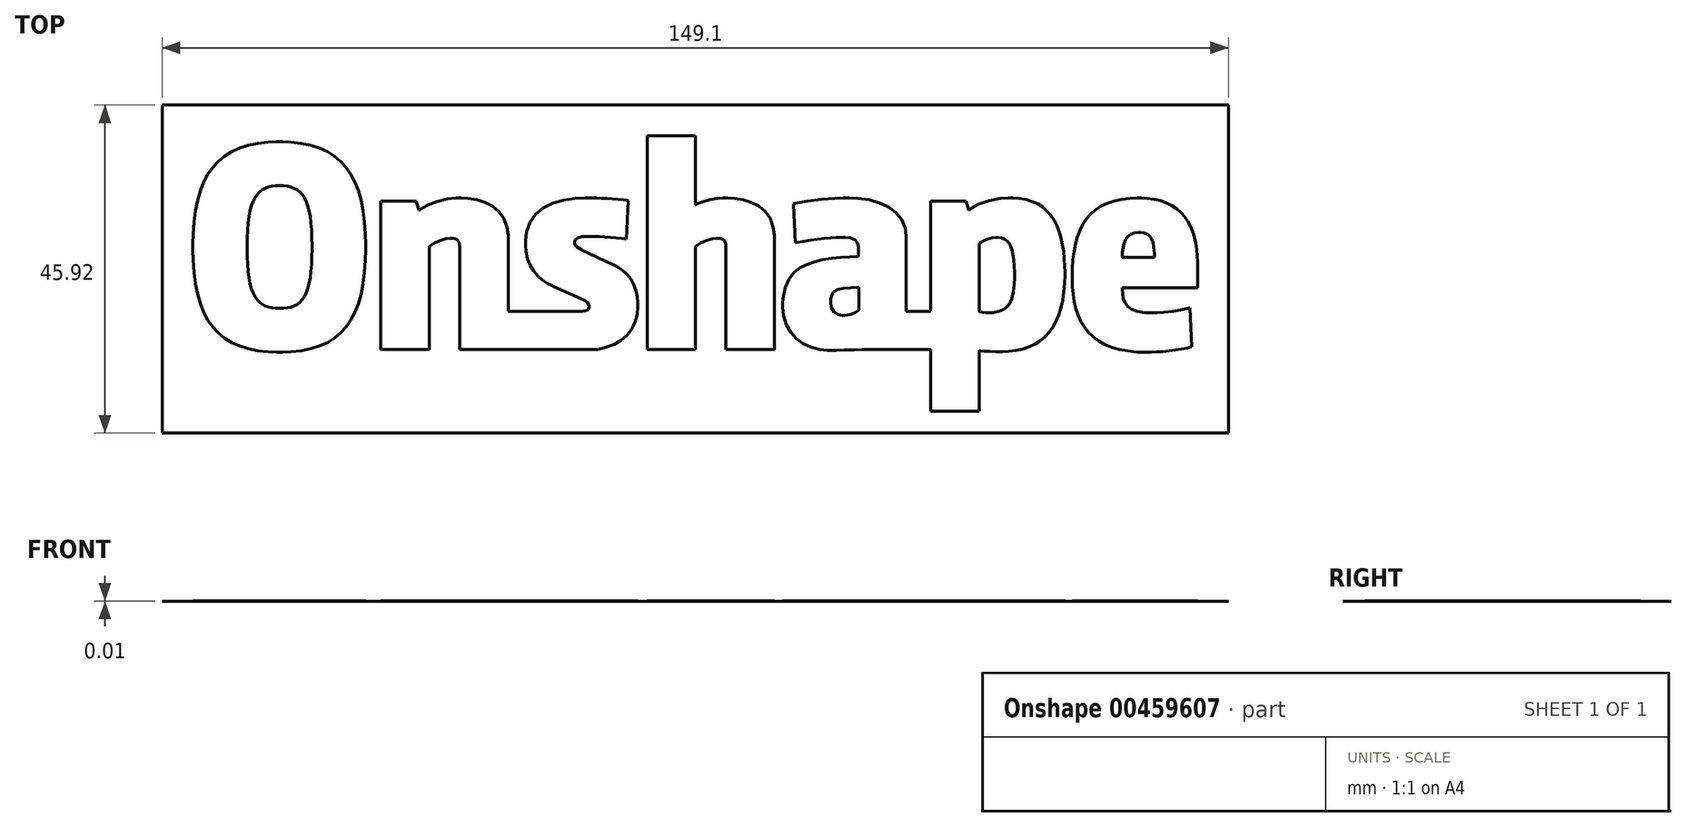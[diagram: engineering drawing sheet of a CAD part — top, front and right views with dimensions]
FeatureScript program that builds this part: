
annotation { "Feature Type Name" : "Feature", "Feature Type Description" : "" }
export const myFeature = defineFeature(function(context is Context, id is Id, definition is map)
    precondition{}
    {
        {
            assignVariable(context, id + "F0", {"name" : "plateHeight", "anyValue" : 1 / 203.2 * mm});
        }
        {
            assignVariable(context, id + "F1", {"name" : "letterHeight", "anyValue" : getVariable(context, 'plateHeight') + (1 / 406.4 * mm)});
        }
        {
            assignVariable(context, id + "F2", {"name" : "scaleFactor", "anyValue" : .226});
        }
        {
            var Q0;
            Q0=qCreatedBy(makeId("Top.planeOp"),FACE);
            var sketch = newSketch(context, id + "F3", { "sketchPlane" : qUnion([Q0])});
            skLineSegment(sketch, "E0", {"start": v(-257.2, 81.58) * mm, "end": v(-258.95, 81.58) * mm});
            skLineSegment(sketch, "E1", {"start": v(-258.95, 81.58) * mm, "end": v(-264.22, 81.33) * mm});
            skLineSegment(sketch, "E2", {"start": v(-264.22, 81.33) * mm, "end": v(-270.7, 80.6) * mm});
            skLineSegment(sketch, "E3", {"start": v(-270.7, 80.6) * mm, "end": v(-276.63, 79.38) * mm});
            skLineSegment(sketch, "E4", {"start": v(-276.63, 79.38) * mm, "end": v(-282.03, 77.66) * mm});
            skLineSegment(sketch, "E5", {"start": v(-282.03, 77.66) * mm, "end": v(-286.92, 75.43) * mm});
            skLineSegment(sketch, "E6", {"start": v(-286.92, 75.43) * mm, "end": v(-291.3, 72.7) * mm});
            skLineSegment(sketch, "E7", {"start": v(-291.3, 72.7) * mm, "end": v(-295.2, 69.45) * mm});
            skLineSegment(sketch, "E8", {"start": v(-295.2, 69.45) * mm, "end": v(-298.64, 65.69) * mm});
            skLineSegment(sketch, "E9", {"start": v(-298.64, 65.69) * mm, "end": v(-301.61, 61.4) * mm});
            skLineSegment(sketch, "E10", {"start": v(-301.61, 61.4) * mm, "end": v(-304.14, 56.58) * mm});
            skLineSegment(sketch, "E11", {"start": v(-304.14, 56.58) * mm, "end": v(-306.24, 51.23) * mm});
            skLineSegment(sketch, "E12", {"start": v(-306.24, 51.23) * mm, "end": v(-307.93, 45.34) * mm});
            skLineSegment(sketch, "E13", {"start": v(-307.93, 45.34) * mm, "end": v(-309.22, 38.91) * mm});
            skLineSegment(sketch, "E14", {"start": v(-309.22, 38.91) * mm, "end": v(-310.12, 31.93) * mm});
            skLineSegment(sketch, "E15", {"start": v(-310.12, 31.93) * mm, "end": v(-310.65, 24.4) * mm});
            skLineSegment(sketch, "E16", {"start": v(-310.65, 24.4) * mm, "end": v(-310.83, 18.34) * mm});
            skLineSegment(sketch, "E17", {"start": v(-310.83, 18.34) * mm, "end": v(-310.83, 16.31) * mm});
            skLineSegment(sketch, "E18", {"start": v(-310.83, 16.31) * mm, "end": v(-310.83, 14.3) * mm});
            skLineSegment(sketch, "E19", {"start": v(-310.83, 14.3) * mm, "end": v(-310.65, 8.23) * mm});
            skLineSegment(sketch, "E20", {"start": v(-310.65, 8.23) * mm, "end": v(-310.12, 0.7) * mm});
            skLineSegment(sketch, "E21", {"start": v(-310.12, 0.7) * mm, "end": v(-309.22, -6.26) * mm});
            skLineSegment(sketch, "E22", {"start": v(-309.22, -6.26) * mm, "end": v(-307.93, -12.69) * mm});
            skLineSegment(sketch, "E23", {"start": v(-307.93, -12.69) * mm, "end": v(-306.24, -18.56) * mm});
            skLineSegment(sketch, "E24", {"start": v(-306.24, -18.56) * mm, "end": v(-304.14, -23.89) * mm});
            skLineSegment(sketch, "E25", {"start": v(-304.14, -23.89) * mm, "end": v(-301.61, -28.7) * mm});
            skLineSegment(sketch, "E26", {"start": v(-301.61, -28.7) * mm, "end": v(-298.64, -32.96) * mm});
            skLineSegment(sketch, "E27", {"start": v(-298.64, -32.96) * mm, "end": v(-295.2, -36.7) * mm});
            skLineSegment(sketch, "E28", {"start": v(-295.2, -36.7) * mm, "end": v(-291.3, -39.94) * mm});
            skLineSegment(sketch, "E29", {"start": v(-291.3, -39.94) * mm, "end": v(-286.92, -42.66) * mm});
            skLineSegment(sketch, "E30", {"start": v(-286.92, -42.66) * mm, "end": v(-282.03, -44.87) * mm});
            skLineSegment(sketch, "E31", {"start": v(-282.03, -44.87) * mm, "end": v(-276.63, -46.58) * mm});
            skLineSegment(sketch, "E32", {"start": v(-276.63, -46.58) * mm, "end": v(-270.7, -47.8) * mm});
            skLineSegment(sketch, "E33", {"start": v(-270.7, -47.8) * mm, "end": v(-264.22, -48.52) * mm});
            skLineSegment(sketch, "E34", {"start": v(-264.22, -48.52) * mm, "end": v(-258.95, -48.76) * mm});
            skLineSegment(sketch, "E35", {"start": v(-258.95, -48.76) * mm, "end": v(-257.2, -48.76) * mm});
            skLineSegment(sketch, "E36", {"start": v(-257.2, -48.76) * mm, "end": v(-255.44, -48.76) * mm});
            skLineSegment(sketch, "E37", {"start": v(-255.44, -48.76) * mm, "end": v(-250.2, -48.52) * mm});
            skLineSegment(sketch, "E38", {"start": v(-250.2, -48.52) * mm, "end": v(-243.76, -47.8) * mm});
            skLineSegment(sketch, "E39", {"start": v(-243.76, -47.8) * mm, "end": v(-237.86, -46.58) * mm});
            skLineSegment(sketch, "E40", {"start": v(-237.86, -46.58) * mm, "end": v(-232.5, -44.87) * mm});
            skLineSegment(sketch, "E41", {"start": v(-232.5, -44.87) * mm, "end": v(-227.64, -42.66) * mm});
            skLineSegment(sketch, "E42", {"start": v(-227.64, -42.66) * mm, "end": v(-223.28, -39.94) * mm});
            skLineSegment(sketch, "E43", {"start": v(-223.28, -39.94) * mm, "end": v(-219.4, -36.7) * mm});
            skLineSegment(sketch, "E44", {"start": v(-219.4, -36.7) * mm, "end": v(-216, -32.96) * mm});
            skLineSegment(sketch, "E45", {"start": v(-216, -32.96) * mm, "end": v(-213.05, -28.7) * mm});
            skLineSegment(sketch, "E46", {"start": v(-213.05, -28.7) * mm, "end": v(-210.55, -23.89) * mm});
            skLineSegment(sketch, "E47", {"start": v(-210.55, -23.89) * mm, "end": v(-208.46, -18.56) * mm});
            skLineSegment(sketch, "E48", {"start": v(-208.46, -18.56) * mm, "end": v(-206.8, -12.69) * mm});
            skLineSegment(sketch, "E49", {"start": v(-206.8, -12.69) * mm, "end": v(-205.52, -6.26) * mm});
            skLineSegment(sketch, "E50", {"start": v(-205.52, -6.26) * mm, "end": v(-204.63, 0.7) * mm});
            skLineSegment(sketch, "E51", {"start": v(-204.63, 0.7) * mm, "end": v(-204.1, 8.23) * mm});
            skLineSegment(sketch, "E52", {"start": v(-204.1, 8.23) * mm, "end": v(-203.93, 14.3) * mm});
            skLineSegment(sketch, "E53", {"start": v(-203.93, 14.3) * mm, "end": v(-203.93, 16.31) * mm});
            skLineSegment(sketch, "E54", {"start": v(-203.93, 16.31) * mm, "end": v(-203.93, 18.34) * mm});
            skLineSegment(sketch, "E55", {"start": v(-203.93, 18.34) * mm, "end": v(-204.1, 24.4) * mm});
            skLineSegment(sketch, "E56", {"start": v(-204.1, 24.4) * mm, "end": v(-204.63, 31.93) * mm});
            skLineSegment(sketch, "E57", {"start": v(-204.63, 31.93) * mm, "end": v(-205.52, 38.91) * mm});
            skLineSegment(sketch, "E58", {"start": v(-205.52, 38.91) * mm, "end": v(-206.8, 45.34) * mm});
            skLineSegment(sketch, "E59", {"start": v(-206.8, 45.34) * mm, "end": v(-208.46, 51.23) * mm});
            skLineSegment(sketch, "E60", {"start": v(-208.46, 51.23) * mm, "end": v(-210.55, 56.58) * mm});
            skLineSegment(sketch, "E61", {"start": v(-210.55, 56.58) * mm, "end": v(-213.05, 61.4) * mm});
            skLineSegment(sketch, "E62", {"start": v(-213.05, 61.4) * mm, "end": v(-216, 65.69) * mm});
            skLineSegment(sketch, "E63", {"start": v(-216, 65.69) * mm, "end": v(-219.4, 69.45) * mm});
            skLineSegment(sketch, "E64", {"start": v(-219.4, 69.45) * mm, "end": v(-223.28, 72.7) * mm});
            skLineSegment(sketch, "E65", {"start": v(-223.28, 72.7) * mm, "end": v(-227.64, 75.43) * mm});
            skLineSegment(sketch, "E66", {"start": v(-227.64, 75.43) * mm, "end": v(-232.5, 77.66) * mm});
            skLineSegment(sketch, "E67", {"start": v(-232.5, 77.66) * mm, "end": v(-237.86, 79.38) * mm});
            skLineSegment(sketch, "E68", {"start": v(-237.86, 79.38) * mm, "end": v(-243.76, 80.6) * mm});
            skLineSegment(sketch, "E69", {"start": v(-243.76, 80.6) * mm, "end": v(-250.2, 81.33) * mm});
            skLineSegment(sketch, "E70", {"start": v(-250.2, 81.33) * mm, "end": v(-255.44, 81.58) * mm});
            skLineSegment(sketch, "E71", {"start": v(-255.44, 81.58) * mm, "end": v(-257.2, 81.58) * mm});
            skLineSegment(sketch, "E72", {"start": v(-257.2, -21.57) * mm, "end": v(-257.83, -21.57) * mm});
            skLineSegment(sketch, "E73", {"start": v(-257.83, -21.57) * mm, "end": v(-259.73, -21.48) * mm});
            skLineSegment(sketch, "E74", {"start": v(-259.73, -21.48) * mm, "end": v(-262.1, -21.2) * mm});
            skLineSegment(sketch, "E75", {"start": v(-262.1, -21.2) * mm, "end": v(-264.27, -20.73) * mm});
            skLineSegment(sketch, "E76", {"start": v(-264.27, -20.73) * mm, "end": v(-266.26, -20) * mm});
            skLineSegment(sketch, "E77", {"start": v(-266.26, -20) * mm, "end": v(-268.08, -19.01) * mm});
            skLineSegment(sketch, "E78", {"start": v(-268.08, -19.01) * mm, "end": v(-269.72, -17.74) * mm});
            skLineSegment(sketch, "E79", {"start": v(-269.72, -17.74) * mm, "end": v(-271.2, -16.15) * mm});
            skLineSegment(sketch, "E80", {"start": v(-271.2, -16.15) * mm, "end": v(-272.5, -14.23) * mm});
            skLineSegment(sketch, "E81", {"start": v(-272.5, -14.23) * mm, "end": v(-273.64, -11.94) * mm});
            skLineSegment(sketch, "E82", {"start": v(-273.64, -11.94) * mm, "end": v(-274.62, -9.27) * mm});
            skLineSegment(sketch, "E83", {"start": v(-274.62, -9.27) * mm, "end": v(-275.44, -6.18) * mm});
            skLineSegment(sketch, "E84", {"start": v(-275.44, -6.18) * mm, "end": v(-276.1, -2.66) * mm});
            skLineSegment(sketch, "E85", {"start": v(-276.1, -2.66) * mm, "end": v(-276.6, 1.33) * mm});
            skLineSegment(sketch, "E86", {"start": v(-276.6, 1.33) * mm, "end": v(-276.97, 5.8) * mm});
            skLineSegment(sketch, "E87", {"start": v(-276.97, 5.8) * mm, "end": v(-277.19, 10.79) * mm});
            skLineSegment(sketch, "E88", {"start": v(-277.19, 10.79) * mm, "end": v(-277.26, 14.93) * mm});
            skLineSegment(sketch, "E89", {"start": v(-277.26, 14.93) * mm, "end": v(-277.26, 16.31) * mm});
            skLineSegment(sketch, "E90", {"start": v(-277.26, 16.31) * mm, "end": v(-277.26, 17.7) * mm});
            skLineSegment(sketch, "E91", {"start": v(-277.26, 17.7) * mm, "end": v(-277.19, 21.84) * mm});
            skLineSegment(sketch, "E92", {"start": v(-277.19, 21.84) * mm, "end": v(-276.97, 26.83) * mm});
            skLineSegment(sketch, "E93", {"start": v(-276.97, 26.83) * mm, "end": v(-276.6, 31.32) * mm});
            skLineSegment(sketch, "E94", {"start": v(-276.6, 31.32) * mm, "end": v(-276.1, 35.32) * mm});
            skLineSegment(sketch, "E95", {"start": v(-276.1, 35.32) * mm, "end": v(-275.44, 38.86) * mm});
            skLineSegment(sketch, "E96", {"start": v(-275.44, 38.86) * mm, "end": v(-274.62, 41.96) * mm});
            skLineSegment(sketch, "E97", {"start": v(-274.62, 41.96) * mm, "end": v(-273.64, 44.65) * mm});
            skLineSegment(sketch, "E98", {"start": v(-273.64, 44.65) * mm, "end": v(-272.5, 46.96) * mm});
            skLineSegment(sketch, "E99", {"start": v(-272.5, 46.96) * mm, "end": v(-271.2, 48.9) * mm});
            skLineSegment(sketch, "E100", {"start": v(-271.2, 48.9) * mm, "end": v(-269.72, 50.5) * mm});
            skLineSegment(sketch, "E101", {"start": v(-269.72, 50.5) * mm, "end": v(-268.08, 51.79) * mm});
            skLineSegment(sketch, "E102", {"start": v(-268.08, 51.79) * mm, "end": v(-266.26, 52.8) * mm});
            skLineSegment(sketch, "E103", {"start": v(-266.26, 52.8) * mm, "end": v(-264.27, 53.52) * mm});
            skLineSegment(sketch, "E104", {"start": v(-264.27, 53.52) * mm, "end": v(-262.1, 54.02) * mm});
            skLineSegment(sketch, "E105", {"start": v(-262.1, 54.02) * mm, "end": v(-259.73, 54.3) * mm});
            skLineSegment(sketch, "E106", {"start": v(-259.73, 54.3) * mm, "end": v(-257.83, 54.39) * mm});
            skLineSegment(sketch, "E107", {"start": v(-257.83, 54.39) * mm, "end": v(-257.2, 54.39) * mm});
            skLineSegment(sketch, "E108", {"start": v(-257.2, 54.39) * mm, "end": v(-256.56, 54.39) * mm});
            skLineSegment(sketch, "E109", {"start": v(-256.56, 54.39) * mm, "end": v(-254.68, 54.3) * mm});
            skLineSegment(sketch, "E110", {"start": v(-254.68, 54.3) * mm, "end": v(-252.34, 54.02) * mm});
            skLineSegment(sketch, "E111", {"start": v(-252.34, 54.02) * mm, "end": v(-250.19, 53.54) * mm});
            skLineSegment(sketch, "E112", {"start": v(-250.19, 53.54) * mm, "end": v(-248.2, 52.82) * mm});
            skLineSegment(sketch, "E113", {"start": v(-248.2, 52.82) * mm, "end": v(-246.39, 51.82) * mm});
            skLineSegment(sketch, "E114", {"start": v(-246.39, 51.82) * mm, "end": v(-244.74, 50.55) * mm});
            skLineSegment(sketch, "E115", {"start": v(-244.74, 50.55) * mm, "end": v(-243.27, 48.95) * mm});
            skLineSegment(sketch, "E116", {"start": v(-243.27, 48.95) * mm, "end": v(-241.95, 47.03) * mm});
            skLineSegment(sketch, "E117", {"start": v(-241.95, 47.03) * mm, "end": v(-240.8, 44.73) * mm});
            skLineSegment(sketch, "E118", {"start": v(-240.8, 44.73) * mm, "end": v(-239.81, 42.04) * mm});
            skLineSegment(sketch, "E119", {"start": v(-239.81, 42.04) * mm, "end": v(-238.98, 38.94) * mm});
            skLineSegment(sketch, "E120", {"start": v(-238.98, 38.94) * mm, "end": v(-238.3, 35.4) * mm});
            skLineSegment(sketch, "E121", {"start": v(-238.3, 35.4) * mm, "end": v(-237.79, 31.39) * mm});
            skLineSegment(sketch, "E122", {"start": v(-237.79, 31.39) * mm, "end": v(-237.42, 26.89) * mm});
            skLineSegment(sketch, "E123", {"start": v(-237.42, 26.89) * mm, "end": v(-237.2, 21.87) * mm});
            skLineSegment(sketch, "E124", {"start": v(-237.2, 21.87) * mm, "end": v(-237.12, 17.7) * mm});
            skLineSegment(sketch, "E125", {"start": v(-237.12, 17.7) * mm, "end": v(-237.12, 16.31) * mm});
            skLineSegment(sketch, "E126", {"start": v(-237.12, 16.31) * mm, "end": v(-237.12, 14.93) * mm});
            skLineSegment(sketch, "E127", {"start": v(-237.12, 14.93) * mm, "end": v(-237.2, 10.76) * mm});
            skLineSegment(sketch, "E128", {"start": v(-237.2, 10.76) * mm, "end": v(-237.42, 5.75) * mm});
            skLineSegment(sketch, "E129", {"start": v(-237.42, 5.75) * mm, "end": v(-237.79, 1.26) * mm});
            skLineSegment(sketch, "E130", {"start": v(-237.79, 1.26) * mm, "end": v(-238.3, -2.74) * mm});
            skLineSegment(sketch, "E131", {"start": v(-238.3, -2.74) * mm, "end": v(-238.98, -6.26) * mm});
            skLineSegment(sketch, "E132", {"start": v(-238.98, -6.26) * mm, "end": v(-239.81, -9.35) * mm});
            skLineSegment(sketch, "E133", {"start": v(-239.81, -9.35) * mm, "end": v(-240.8, -12.02) * mm});
            skLineSegment(sketch, "E134", {"start": v(-240.8, -12.02) * mm, "end": v(-241.95, -14.3) * mm});
            skLineSegment(sketch, "E135", {"start": v(-241.95, -14.3) * mm, "end": v(-243.27, -16.22) * mm});
            skLineSegment(sketch, "E136", {"start": v(-243.27, -16.22) * mm, "end": v(-244.74, -17.79) * mm});
            skLineSegment(sketch, "E137", {"start": v(-244.74, -17.79) * mm, "end": v(-246.39, -19.05) * mm});
            skLineSegment(sketch, "E138", {"start": v(-246.39, -19.05) * mm, "end": v(-248.2, -20.03) * mm});
            skLineSegment(sketch, "E139", {"start": v(-248.2, -20.03) * mm, "end": v(-250.19, -20.74) * mm});
            skLineSegment(sketch, "E140", {"start": v(-250.19, -20.74) * mm, "end": v(-252.34, -21.22) * mm});
            skLineSegment(sketch, "E141", {"start": v(-252.34, -21.22) * mm, "end": v(-254.68, -21.48) * mm});
            skLineSegment(sketch, "E142", {"start": v(-254.68, -21.48) * mm, "end": v(-256.56, -21.57) * mm});
            skLineSegment(sketch, "E143", {"start": v(-256.56, -21.57) * mm, "end": v(-257.2, -21.57) * mm});
            skLineSegment(sketch, "E144", {"start": v(18.58, 46.88) * mm, "end": v(17.34, 46.88) * mm});
            skLineSegment(sketch, "E145", {"start": v(17.34, 46.88) * mm, "end": v(13.62, 46.58) * mm});
            skLineSegment(sketch, "E146", {"start": v(13.62, 46.58) * mm, "end": v(8.78, 45.71) * mm});
            skLineSegment(sketch, "E147", {"start": v(8.78, 45.71) * mm, "end": v(4.28, 44.35) * mm});
            skLineSegment(sketch, "E148", {"start": v(4.28, 44.35) * mm, "end": v(1.32, 43.1) * mm});
            skLineSegment(sketch, "E149", {"start": v(1.32, 43.1) * mm, "end": v(0.39, 42.57) * mm});
            skLineSegment(sketch, "E150", {"start": v(0.39, 42.57) * mm, "end": v(0.2, 42.57) * mm});
            skLineSegment(sketch, "E151", {"start": v(0.2, 42.57) * mm, "end": v(0.2, 85.33) * mm});
            skLineSegment(sketch, "E152", {"start": v(0.2, 85.33) * mm, "end": v(-29.8, 85.33) * mm});
            skLineSegment(sketch, "E153", {"start": v(-29.8, 85.33) * mm, "end": v(-29.8, -46.88) * mm});
            skLineSegment(sketch, "E154", {"start": v(-29.8, -46.88) * mm, "end": v(0.2, -46.88) * mm});
            skLineSegment(sketch, "E155", {"start": v(0.2, -46.88) * mm, "end": v(0.2, 16.88) * mm});
            skLineSegment(sketch, "E156", {"start": v(0.2, 16.88) * mm, "end": v(0.98, 17.45) * mm});
            skLineSegment(sketch, "E157", {"start": v(0.98, 17.45) * mm, "end": v(3.47, 18.93) * mm});
            skLineSegment(sketch, "E158", {"start": v(3.47, 18.93) * mm, "end": v(6.95, 20.54) * mm});
            skLineSegment(sketch, "E159", {"start": v(6.95, 20.54) * mm, "end": v(10.43, 21.57) * mm});
            skLineSegment(sketch, "E160", {"start": v(10.43, 21.57) * mm, "end": v(12.88, 21.94) * mm});
            skLineSegment(sketch, "E161", {"start": v(12.88, 21.94) * mm, "end": v(13.7, 21.94) * mm});
            skLineSegment(sketch, "E162", {"start": v(13.7, 21.94) * mm, "end": v(14.03, 21.94) * mm});
            skLineSegment(sketch, "E163", {"start": v(14.03, 21.94) * mm, "end": v(15, 21.87) * mm});
            skLineSegment(sketch, "E164", {"start": v(15, 21.87) * mm, "end": v(16.1, 21.65) * mm});
            skLineSegment(sketch, "E165", {"start": v(16.1, 21.65) * mm, "end": v(17.01, 21.27) * mm});
            skLineSegment(sketch, "E166", {"start": v(17.01, 21.27) * mm, "end": v(17.73, 20.72) * mm});
            skLineSegment(sketch, "E167", {"start": v(17.73, 20.72) * mm, "end": v(18.28, 20) * mm});
            skLineSegment(sketch, "E168", {"start": v(18.28, 20) * mm, "end": v(18.66, 19.1) * mm});
            skLineSegment(sketch, "E169", {"start": v(18.66, 19.1) * mm, "end": v(18.88, 18) * mm});
            skLineSegment(sketch, "E170", {"start": v(18.88, 18) * mm, "end": v(18.95, 17.02) * mm});
            skLineSegment(sketch, "E171", {"start": v(18.95, 17.02) * mm, "end": v(18.95, 16.7) * mm});
            skLineSegment(sketch, "E172", {"start": v(18.95, 16.7) * mm, "end": v(18.95, -46.88) * mm});
            skLineSegment(sketch, "E173", {"start": v(18.95, -46.88) * mm, "end": v(48.96, -46.88) * mm});
            skLineSegment(sketch, "E174", {"start": v(48.96, -46.88) * mm, "end": v(48.96, 22.13) * mm});
            skLineSegment(sketch, "E175", {"start": v(48.96, 22.13) * mm, "end": v(48.96, 23.77) * mm});
            skLineSegment(sketch, "E176", {"start": v(48.96, 23.77) * mm, "end": v(48.27, 28.69) * mm});
            skLineSegment(sketch, "E177", {"start": v(48.27, 28.69) * mm, "end": v(46.32, 34.07) * mm});
            skLineSegment(sketch, "E178", {"start": v(46.32, 34.07) * mm, "end": v(43.3, 38.37) * mm});
            skLineSegment(sketch, "E179", {"start": v(43.3, 38.37) * mm, "end": v(39.4, 41.68) * mm});
            skLineSegment(sketch, "E180", {"start": v(39.4, 41.68) * mm, "end": v(34.78, 44.1) * mm});
            skLineSegment(sketch, "E181", {"start": v(34.78, 44.1) * mm, "end": v(29.65, 45.7) * mm});
            skLineSegment(sketch, "E182", {"start": v(29.65, 45.7) * mm, "end": v(24.2, 46.6) * mm});
            skLineSegment(sketch, "E183", {"start": v(24.2, 46.6) * mm, "end": v(19.98, 46.88) * mm});
            skLineSegment(sketch, "E184", {"start": v(19.98, 46.88) * mm, "end": v(18.58, 46.88) * mm});
            skLineSegment(sketch, "E185", {"start": v(274.82, 46.88) * mm, "end": v(273.4, 46.88) * mm});
            skLineSegment(sketch, "E186", {"start": v(273.4, 46.88) * mm, "end": v(269.13, 46.67) * mm});
            skLineSegment(sketch, "E187", {"start": v(269.13, 46.67) * mm, "end": v(263.93, 46.05) * mm});
            skLineSegment(sketch, "E188", {"start": v(263.93, 46.05) * mm, "end": v(259.2, 45.02) * mm});
            skLineSegment(sketch, "E189", {"start": v(259.2, 45.02) * mm, "end": v(254.94, 43.58) * mm});
            skLineSegment(sketch, "E190", {"start": v(254.94, 43.58) * mm, "end": v(251.12, 41.75) * mm});
            skLineSegment(sketch, "E191", {"start": v(251.12, 41.75) * mm, "end": v(247.72, 39.53) * mm});
            skLineSegment(sketch, "E192", {"start": v(247.72, 39.53) * mm, "end": v(244.72, 36.92) * mm});
            skLineSegment(sketch, "E193", {"start": v(244.72, 36.92) * mm, "end": v(242.12, 33.95) * mm});
            skLineSegment(sketch, "E194", {"start": v(242.12, 33.95) * mm, "end": v(239.88, 30.6) * mm});
            skLineSegment(sketch, "E195", {"start": v(239.88, 30.6) * mm, "end": v(238, 26.89) * mm});
            skLineSegment(sketch, "E196", {"start": v(238, 26.89) * mm, "end": v(236.46, 22.82) * mm});
            skLineSegment(sketch, "E197", {"start": v(236.46, 22.82) * mm, "end": v(235.23, 18.4) * mm});
            skLineSegment(sketch, "E198", {"start": v(235.23, 18.4) * mm, "end": v(234.31, 13.64) * mm});
            skLineSegment(sketch, "E199", {"start": v(234.31, 13.64) * mm, "end": v(233.68, 8.55) * mm});
            skLineSegment(sketch, "E200", {"start": v(233.68, 8.55) * mm, "end": v(233.3, 3.12) * mm});
            skLineSegment(sketch, "E201", {"start": v(233.3, 3.12) * mm, "end": v(233.18, -1.2) * mm});
            skLineSegment(sketch, "E202", {"start": v(233.18, -1.2) * mm, "end": v(233.18, -2.63) * mm});
            skLineSegment(sketch, "E203", {"start": v(233.18, -2.63) * mm, "end": v(233.18, -3.94) * mm});
            skLineSegment(sketch, "E204", {"start": v(233.18, -3.94) * mm, "end": v(233.32, -7.87) * mm});
            skLineSegment(sketch, "E205", {"start": v(233.32, -7.87) * mm, "end": v(233.75, -12.85) * mm});
            skLineSegment(sketch, "E206", {"start": v(233.75, -12.85) * mm, "end": v(234.47, -17.54) * mm});
            skLineSegment(sketch, "E207", {"start": v(234.47, -17.54) * mm, "end": v(235.52, -21.94) * mm});
            skLineSegment(sketch, "E208", {"start": v(235.52, -21.94) * mm, "end": v(236.9, -26.04) * mm});
            skLineSegment(sketch, "E209", {"start": v(236.9, -26.04) * mm, "end": v(238.65, -29.83) * mm});
            skLineSegment(sketch, "E210", {"start": v(238.65, -29.83) * mm, "end": v(240.76, -33.3) * mm});
            skLineSegment(sketch, "E211", {"start": v(240.76, -33.3) * mm, "end": v(243.27, -36.45) * mm});
            skLineSegment(sketch, "E212", {"start": v(243.27, -36.45) * mm, "end": v(246.18, -39.26) * mm});
            skLineSegment(sketch, "E213", {"start": v(246.18, -39.26) * mm, "end": v(249.52, -41.73) * mm});
            skLineSegment(sketch, "E214", {"start": v(249.52, -41.73) * mm, "end": v(253.3, -43.84) * mm});
            skLineSegment(sketch, "E215", {"start": v(253.3, -43.84) * mm, "end": v(257.55, -45.58) * mm});
            skLineSegment(sketch, "E216", {"start": v(257.55, -45.58) * mm, "end": v(262.28, -46.96) * mm});
            skLineSegment(sketch, "E217", {"start": v(262.28, -46.96) * mm, "end": v(267.5, -47.96) * mm});
            skLineSegment(sketch, "E218", {"start": v(267.5, -47.96) * mm, "end": v(273.24, -48.56) * mm});
            skLineSegment(sketch, "E219", {"start": v(273.24, -48.56) * mm, "end": v(277.94, -48.76) * mm});
            skLineSegment(sketch, "E220", {"start": v(277.94, -48.76) * mm, "end": v(279.5, -48.76) * mm});
            skLineSegment(sketch, "E221", {"start": v(279.5, -48.76) * mm, "end": v(280.2, -48.76) * mm});
            skLineSegment(sketch, "E222", {"start": v(280.2, -48.76) * mm, "end": v(282.24, -48.7) * mm});
            skLineSegment(sketch, "E223", {"start": v(282.24, -48.7) * mm, "end": v(285.53, -48.55) * mm});
            skLineSegment(sketch, "E224", {"start": v(285.53, -48.55) * mm, "end": v(289.21, -48.28) * mm});
            skLineSegment(sketch, "E225", {"start": v(289.21, -48.28) * mm, "end": v(293.1, -47.9) * mm});
            skLineSegment(sketch, "E226", {"start": v(293.1, -47.9) * mm, "end": v(297.03, -47.4) * mm});
            skLineSegment(sketch, "E227", {"start": v(297.03, -47.4) * mm, "end": v(300.82, -46.78) * mm});
            skLineSegment(sketch, "E228", {"start": v(300.82, -46.78) * mm, "end": v(304.29, -46.05) * mm});
            skLineSegment(sketch, "E229", {"start": v(304.29, -46.05) * mm, "end": v(306.53, -45.45) * mm});
            skLineSegment(sketch, "E230", {"start": v(306.53, -45.45) * mm, "end": v(307.26, -45.2) * mm});
            skLineSegment(sketch, "E231", {"start": v(307.26, -45.2) * mm, "end": v(306.14, -21.2) * mm});
            skLineSegment(sketch, "E232", {"start": v(306.14, -21.2) * mm, "end": v(304.98, -21.52) * mm});
            skLineSegment(sketch, "E233", {"start": v(304.98, -21.52) * mm, "end": v(301.45, -22.32) * mm});
            skLineSegment(sketch, "E234", {"start": v(301.45, -22.32) * mm, "end": v(295.75, -23.35) * mm});
            skLineSegment(sketch, "E235", {"start": v(295.75, -23.35) * mm, "end": v(289.81, -24.1) * mm});
            skLineSegment(sketch, "E236", {"start": v(289.81, -24.1) * mm, "end": v(285.74, -24.38) * mm});
            skLineSegment(sketch, "E237", {"start": v(285.74, -24.38) * mm, "end": v(284.38, -24.38) * mm});
            skLineSegment(sketch, "E238", {"start": v(284.38, -24.38) * mm, "end": v(282.85, -24.38) * mm});
            skLineSegment(sketch, "E239", {"start": v(282.85, -24.38) * mm, "end": v(278.24, -24.13) * mm});
            skLineSegment(sketch, "E240", {"start": v(278.24, -24.13) * mm, "end": v(273.5, -23.37) * mm});
            skLineSegment(sketch, "E241", {"start": v(273.5, -23.37) * mm, "end": v(269.96, -22.12) * mm});
            skLineSegment(sketch, "E242", {"start": v(269.96, -22.12) * mm, "end": v(267.46, -20.4) * mm});
            skLineSegment(sketch, "E243", {"start": v(267.46, -20.4) * mm, "end": v(265.82, -18.19) * mm});
            skLineSegment(sketch, "E244", {"start": v(265.82, -18.19) * mm, "end": v(264.87, -15.52) * mm});
            skLineSegment(sketch, "E245", {"start": v(264.87, -15.52) * mm, "end": v(264.42, -12.4) * mm});
            skLineSegment(sketch, "E246", {"start": v(264.42, -12.4) * mm, "end": v(264.32, -9.7) * mm});
            skLineSegment(sketch, "E247", {"start": v(264.32, -9.7) * mm, "end": v(264.32, -8.82) * mm});
            skLineSegment(sketch, "E248", {"start": v(264.32, -8.82) * mm, "end": v(310.83, -8.82) * mm});
            skLineSegment(sketch, "E249", {"start": v(310.83, -8.82) * mm, "end": v(310.83, 6.56) * mm});
            skLineSegment(sketch, "E250", {"start": v(310.83, 6.56) * mm, "end": v(310.83, 7.62) * mm});
            skLineSegment(sketch, "E251", {"start": v(310.83, 7.62) * mm, "end": v(310.71, 10.79) * mm});
            skLineSegment(sketch, "E252", {"start": v(310.71, 10.79) * mm, "end": v(310.37, 14.86) * mm});
            skLineSegment(sketch, "E253", {"start": v(310.37, 14.86) * mm, "end": v(309.77, 18.78) * mm});
            skLineSegment(sketch, "E254", {"start": v(309.77, 18.78) * mm, "end": v(308.92, 22.52) * mm});
            skLineSegment(sketch, "E255", {"start": v(308.92, 22.52) * mm, "end": v(307.8, 26.05) * mm});
            skLineSegment(sketch, "E256", {"start": v(307.8, 26.05) * mm, "end": v(306.4, 29.38) * mm});
            skLineSegment(sketch, "E257", {"start": v(306.4, 29.38) * mm, "end": v(304.72, 32.47) * mm});
            skLineSegment(sketch, "E258", {"start": v(304.72, 32.47) * mm, "end": v(302.74, 35.3) * mm});
            skLineSegment(sketch, "E259", {"start": v(302.74, 35.3) * mm, "end": v(300.44, 37.88) * mm});
            skLineSegment(sketch, "E260", {"start": v(300.44, 37.88) * mm, "end": v(297.83, 40.16) * mm});
            skLineSegment(sketch, "E261", {"start": v(297.83, 40.16) * mm, "end": v(294.89, 42.14) * mm});
            skLineSegment(sketch, "E262", {"start": v(294.89, 42.14) * mm, "end": v(291.6, 43.8) * mm});
            skLineSegment(sketch, "E263", {"start": v(291.6, 43.8) * mm, "end": v(287.96, 45.12) * mm});
            skLineSegment(sketch, "E264", {"start": v(287.96, 45.12) * mm, "end": v(283.96, 46.1) * mm});
            skLineSegment(sketch, "E265", {"start": v(283.96, 46.1) * mm, "end": v(279.58, 46.68) * mm});
            skLineSegment(sketch, "E266", {"start": v(279.58, 46.68) * mm, "end": v(276.01, 46.88) * mm});
            skLineSegment(sketch, "E267", {"start": v(276.01, 46.88) * mm, "end": v(274.82, 46.88) * mm});
            skLineSegment(sketch, "E268", {"start": v(284.01, 10.13) * mm, "end": v(264.13, 10.13) * mm});
            skLineSegment(sketch, "E269", {"start": v(264.13, 10.13) * mm, "end": v(264.16, 10.91) * mm});
            skLineSegment(sketch, "E270", {"start": v(264.16, 10.91) * mm, "end": v(264.33, 13.27) * mm});
            skLineSegment(sketch, "E271", {"start": v(264.33, 13.27) * mm, "end": v(264.7, 16.17) * mm});
            skLineSegment(sketch, "E272", {"start": v(264.7, 16.17) * mm, "end": v(265.31, 18.78) * mm});
            skLineSegment(sketch, "E273", {"start": v(265.31, 18.78) * mm, "end": v(266.26, 21.05) * mm});
            skLineSegment(sketch, "E274", {"start": v(266.26, 21.05) * mm, "end": v(267.62, 22.91) * mm});
            skLineSegment(sketch, "E275", {"start": v(267.62, 22.91) * mm, "end": v(269.48, 24.31) * mm});
            skLineSegment(sketch, "E276", {"start": v(269.48, 24.31) * mm, "end": v(271.91, 25.2) * mm});
            skLineSegment(sketch, "E277", {"start": v(271.91, 25.2) * mm, "end": v(274.23, 25.5) * mm});
            skLineSegment(sketch, "E278", {"start": v(274.23, 25.5) * mm, "end": v(275, 25.5) * mm});
            skLineSegment(sketch, "E279", {"start": v(275, 25.5) * mm, "end": v(275.66, 25.5) * mm});
            skLineSegment(sketch, "E280", {"start": v(275.66, 25.5) * mm, "end": v(277.6, 25.2) * mm});
            skLineSegment(sketch, "E281", {"start": v(277.6, 25.2) * mm, "end": v(279.66, 24.31) * mm});
            skLineSegment(sketch, "E282", {"start": v(279.66, 24.31) * mm, "end": v(281.24, 22.95) * mm});
            skLineSegment(sketch, "E283", {"start": v(281.24, 22.95) * mm, "end": v(282.4, 21.2) * mm});
            skLineSegment(sketch, "E284", {"start": v(282.4, 21.2) * mm, "end": v(283.19, 19.11) * mm});
            skLineSegment(sketch, "E285", {"start": v(283.19, 19.11) * mm, "end": v(283.69, 16.8) * mm});
            skLineSegment(sketch, "E286", {"start": v(283.69, 16.8) * mm, "end": v(283.94, 14.34) * mm});
            skLineSegment(sketch, "E287", {"start": v(283.94, 14.34) * mm, "end": v(284.01, 12.45) * mm});
            skLineSegment(sketch, "E288", {"start": v(284.01, 12.45) * mm, "end": v(284.01, 11.81) * mm});
            skLineSegment(sketch, "E289", {"start": v(284.01, 11.81) * mm, "end": v(284.01, 10.13) * mm});
            skLineSegment(sketch, "E290", {"start": v(-50.92, 5.62) * mm, "end": v(-70.05, 14.63) * mm});
            skLineSegment(sketch, "E291", {"start": v(-70.05, 14.63) * mm, "end": v(-70.53, 14.85) * mm});
            skLineSegment(sketch, "E292", {"start": v(-70.53, 14.85) * mm, "end": v(-71.94, 15.54) * mm});
            skLineSegment(sketch, "E293", {"start": v(-71.94, 15.54) * mm, "end": v(-73.35, 16.48) * mm});
            skLineSegment(sketch, "E294", {"start": v(-73.35, 16.48) * mm, "end": v(-74.24, 17.66) * mm});
            skLineSegment(sketch, "E295", {"start": v(-74.24, 17.66) * mm, "end": v(-74.55, 18.9) * mm});
            skLineSegment(sketch, "E296", {"start": v(-74.55, 18.9) * mm, "end": v(-74.55, 19.32) * mm});
            skLineSegment(sketch, "E297", {"start": v(-74.55, 19.32) * mm, "end": v(-74.55, 19.76) * mm});
            skLineSegment(sketch, "E298", {"start": v(-74.55, 19.76) * mm, "end": v(-74.11, 21.1) * mm});
            skLineSegment(sketch, "E299", {"start": v(-74.11, 21.1) * mm, "end": v(-72.63, 22.25) * mm});
            skLineSegment(sketch, "E300", {"start": v(-72.63, 22.25) * mm, "end": v(-69.8, 22.87) * mm});
            skLineSegment(sketch, "E301", {"start": v(-69.8, 22.87) * mm, "end": v(-66.47, 23.06) * mm});
            skLineSegment(sketch, "E302", {"start": v(-66.47, 23.06) * mm, "end": v(-65.36, 23.06) * mm});
            skLineSegment(sketch, "E303", {"start": v(-65.36, 23.06) * mm, "end": v(-65.02, 23.06) * mm});
            skLineSegment(sketch, "E304", {"start": v(-65.02, 23.06) * mm, "end": v(-64, 23.05) * mm});
            skLineSegment(sketch, "E305", {"start": v(-64, 23.05) * mm, "end": v(-61.87, 22.99) * mm});
            skLineSegment(sketch, "E306", {"start": v(-61.87, 22.99) * mm, "end": v(-59.14, 22.88) * mm});
            skLineSegment(sketch, "E307", {"start": v(-59.14, 22.88) * mm, "end": v(-55.98, 22.72) * mm});
            skLineSegment(sketch, "E308", {"start": v(-55.98, 22.72) * mm, "end": v(-52.59, 22.5) * mm});
            skLineSegment(sketch, "E309", {"start": v(-52.59, 22.5) * mm, "end": v(-49.12, 22.2) * mm});
            skLineSegment(sketch, "E310", {"start": v(-49.12, 22.2) * mm, "end": v(-45.75, 21.83) * mm});
            skLineSegment(sketch, "E311", {"start": v(-45.75, 21.83) * mm, "end": v(-43.44, 21.5) * mm});
            skLineSegment(sketch, "E312", {"start": v(-43.44, 21.5) * mm, "end": v(-42.67, 21.38) * mm});
            skLineSegment(sketch, "E313", {"start": v(-42.67, 21.38) * mm, "end": v(-41.54, 45.2) * mm});
            skLineSegment(sketch, "E314", {"start": v(-41.54, 45.2) * mm, "end": v(-42.3, 45.33) * mm});
            skLineSegment(sketch, "E315", {"start": v(-42.3, 45.33) * mm, "end": v(-44.6, 45.65) * mm});
            skLineSegment(sketch, "E316", {"start": v(-44.6, 45.65) * mm, "end": v(-47.91, 46.01) * mm});
            skLineSegment(sketch, "E317", {"start": v(-47.91, 46.01) * mm, "end": v(-51.36, 46.3) * mm});
            skLineSegment(sketch, "E318", {"start": v(-51.36, 46.3) * mm, "end": v(-54.81, 46.53) * mm});
            skLineSegment(sketch, "E319", {"start": v(-54.81, 46.53) * mm, "end": v(-58.14, 46.7) * mm});
            skLineSegment(sketch, "E320", {"start": v(-58.14, 46.7) * mm, "end": v(-61.22, 46.8) * mm});
            skLineSegment(sketch, "E321", {"start": v(-61.22, 46.8) * mm, "end": v(-63.92, 46.86) * mm});
            skLineSegment(sketch, "E322", {"start": v(-63.92, 46.86) * mm, "end": v(-65.56, 46.88) * mm});
            skLineSegment(sketch, "E323", {"start": v(-65.56, 46.88) * mm, "end": v(-66.11, 46.88) * mm});
            skLineSegment(sketch, "E324", {"start": v(-66.11, 46.88) * mm, "end": v(-68.16, 46.88) * mm});
            skLineSegment(sketch, "E325", {"start": v(-68.16, 46.88) * mm, "end": v(-74.3, 46.52) * mm});
            skLineSegment(sketch, "E326", {"start": v(-74.3, 46.52) * mm, "end": v(-81.78, 45.39) * mm});
            skLineSegment(sketch, "E327", {"start": v(-81.78, 45.39) * mm, "end": v(-88.42, 43.42) * mm});
            skLineSegment(sketch, "E328", {"start": v(-88.42, 43.42) * mm, "end": v(-94.12, 40.56) * mm});
            skLineSegment(sketch, "E329", {"start": v(-94.12, 40.56) * mm, "end": v(-98.76, 36.72) * mm});
            skLineSegment(sketch, "E330", {"start": v(-98.76, 36.72) * mm, "end": v(-102.21, 31.85) * mm});
            skLineSegment(sketch, "E331", {"start": v(-102.21, 31.85) * mm, "end": v(-104.37, 25.88) * mm});
            skLineSegment(sketch, "E332", {"start": v(-104.37, 25.88) * mm, "end": v(-105.12, 20.54) * mm});
            skLineSegment(sketch, "E333", {"start": v(-105.12, 20.54) * mm, "end": v(-105.12, 18.75) * mm});
            skLineSegment(sketch, "E334", {"start": v(-105.12, 18.75) * mm, "end": v(-105.12, 17.5) * mm});
            skLineSegment(sketch, "E335", {"start": v(-105.12, 17.5) * mm, "end": v(-104.77, 13.74) * mm});
            skLineSegment(sketch, "E336", {"start": v(-104.77, 13.74) * mm, "end": v(-103.77, 9.24) * mm});
            skLineSegment(sketch, "E337", {"start": v(-103.77, 9.24) * mm, "end": v(-102.18, 5.23) * mm});
            skLineSegment(sketch, "E338", {"start": v(-102.18, 5.23) * mm, "end": v(-100.08, 1.71) * mm});
            skLineSegment(sketch, "E339", {"start": v(-100.08, 1.71) * mm, "end": v(-97.53, -1.35) * mm});
            skLineSegment(sketch, "E340", {"start": v(-97.53, -1.35) * mm, "end": v(-94.6, -3.95) * mm});
            skLineSegment(sketch, "E341", {"start": v(-94.6, -3.95) * mm, "end": v(-91.35, -6.12) * mm});
            skLineSegment(sketch, "E342", {"start": v(-91.35, -6.12) * mm, "end": v(-88.76, -7.5) * mm});
            skLineSegment(sketch, "E343", {"start": v(-88.76, -7.5) * mm, "end": v(-87.86, -7.88) * mm});
            skLineSegment(sketch, "E344", {"start": v(-87.86, -7.88) * mm, "end": v(-70.61, -15.57) * mm});
            skLineSegment(sketch, "E345", {"start": v(-70.61, -15.57) * mm, "end": v(-70.05, -15.82) * mm});
            skLineSegment(sketch, "E346", {"start": v(-70.05, -15.82) * mm, "end": v(-68.43, -16.7) * mm});
            skLineSegment(sketch, "E347", {"start": v(-68.43, -16.7) * mm, "end": v(-66.9, -17.86) * mm});
            skLineSegment(sketch, "E348", {"start": v(-66.9, -17.86) * mm, "end": v(-66.02, -19.1) * mm});
            skLineSegment(sketch, "E349", {"start": v(-66.02, -19.1) * mm, "end": v(-65.74, -20.1) * mm});
            skLineSegment(sketch, "E350", {"start": v(-65.74, -20.1) * mm, "end": v(-65.74, -20.44) * mm});
            skLineSegment(sketch, "E351", {"start": v(-65.74, -20.44) * mm, "end": v(-65.74, -20.69) * mm});
            skLineSegment(sketch, "E352", {"start": v(-65.74, -20.69) * mm, "end": v(-65.83, -21.43) * mm});
            skLineSegment(sketch, "E353", {"start": v(-65.83, -21.43) * mm, "end": v(-66.13, -22.16) * mm});
            skLineSegment(sketch, "E354", {"start": v(-66.13, -22.16) * mm, "end": v(-66.68, -22.67) * mm});
            skLineSegment(sketch, "E355", {"start": v(-66.68, -22.67) * mm, "end": v(-67.51, -23) * mm});
            skLineSegment(sketch, "E356", {"start": v(-67.51, -23) * mm, "end": v(-68.66, -23.2) * mm});
            skLineSegment(sketch, "E357", {"start": v(-68.66, -23.2) * mm, "end": v(-70.16, -23.29) * mm});
            skLineSegment(sketch, "E358", {"start": v(-70.16, -23.29) * mm, "end": v(-72.05, -23.31) * mm});
            skLineSegment(sketch, "E359", {"start": v(-72.05, -23.31) * mm, "end": v(-73.78, -23.31) * mm});
            skLineSegment(sketch, "E360", {"start": v(-73.78, -23.31) * mm, "end": v(-74.35, -23.31) * mm});
            skLineSegment(sketch, "E361", {"start": v(-74.35, -23.31) * mm, "end": v(-75.54, -23.31) * mm});
            skLineSegment(sketch, "E362", {"start": v(-75.54, -23.31) * mm, "end": v(-79.08, -23.31) * mm});
            skLineSegment(sketch, "E363", {"start": v(-79.08, -23.31) * mm, "end": v(-85.3, -23.31) * mm});
            skLineSegment(sketch, "E364", {"start": v(-85.3, -23.31) * mm, "end": v(-92.47, -23.31) * mm});
            skLineSegment(sketch, "E365", {"start": v(-92.47, -23.31) * mm, "end": v(-98.18, -23.32) * mm});
            skLineSegment(sketch, "E366", {"start": v(-98.18, -23.32) * mm, "end": v(-100.08, -23.32) * mm});
            skLineSegment(sketch, "E367", {"start": v(-100.08, -23.32) * mm, "end": v(-100.08, -23.31) * mm});
            skLineSegment(sketch, "E368", {"start": v(-100.08, -23.31) * mm, "end": v(-115.81, -23.31) * mm});
            skLineSegment(sketch, "E369", {"start": v(-115.81, -23.31) * mm, "end": v(-115.81, 22.13) * mm});
            skLineSegment(sketch, "E370", {"start": v(-115.81, 22.13) * mm, "end": v(-115.81, 23.77) * mm});
            skLineSegment(sketch, "E371", {"start": v(-115.81, 23.77) * mm, "end": v(-116.5, 28.69) * mm});
            skLineSegment(sketch, "E372", {"start": v(-116.5, 28.69) * mm, "end": v(-118.45, 34.07) * mm});
            skLineSegment(sketch, "E373", {"start": v(-118.45, 34.07) * mm, "end": v(-121.47, 38.37) * mm});
            skLineSegment(sketch, "E374", {"start": v(-121.47, 38.37) * mm, "end": v(-125.38, 41.68) * mm});
            skLineSegment(sketch, "E375", {"start": v(-125.38, 41.68) * mm, "end": v(-129.99, 44.1) * mm});
            skLineSegment(sketch, "E376", {"start": v(-129.99, 44.1) * mm, "end": v(-135.12, 45.7) * mm});
            skLineSegment(sketch, "E377", {"start": v(-135.12, 45.7) * mm, "end": v(-140.58, 46.6) * mm});
            skLineSegment(sketch, "E378", {"start": v(-140.58, 46.6) * mm, "end": v(-144.8, 46.88) * mm});
            skLineSegment(sketch, "E379", {"start": v(-144.8, 46.88) * mm, "end": v(-146.2, 46.88) * mm});
            skLineSegment(sketch, "E380", {"start": v(-146.2, 46.88) * mm, "end": v(-147.97, 46.88) * mm});
            skLineSegment(sketch, "E381", {"start": v(-147.97, 46.88) * mm, "end": v(-153.3, 46.29) * mm});
            skLineSegment(sketch, "E382", {"start": v(-153.3, 46.29) * mm, "end": v(-159.88, 44.65) * mm});
            skLineSegment(sketch, "E383", {"start": v(-159.88, 44.65) * mm, "end": v(-165.76, 42.21) * mm});
            skLineSegment(sketch, "E384", {"start": v(-165.76, 42.21) * mm, "end": v(-169.58, 40.04) * mm});
            skLineSegment(sketch, "E385", {"start": v(-169.58, 40.04) * mm, "end": v(-170.76, 39.2) * mm});
            skLineSegment(sketch, "E386", {"start": v(-170.76, 39.2) * mm, "end": v(-170.95, 39.2) * mm});
            skLineSegment(sketch, "E387", {"start": v(-170.95, 39.2) * mm, "end": v(-172.63, 45) * mm});
            skLineSegment(sketch, "E388", {"start": v(-172.63, 45) * mm, "end": v(-194.58, 45) * mm});
            skLineSegment(sketch, "E389", {"start": v(-194.58, 45) * mm, "end": v(-194.58, -46.88) * mm});
            skLineSegment(sketch, "E390", {"start": v(-194.58, -46.88) * mm, "end": v(-164.57, -46.88) * mm});
            skLineSegment(sketch, "E391", {"start": v(-164.57, -46.88) * mm, "end": v(-164.57, 16.88) * mm});
            skLineSegment(sketch, "E392", {"start": v(-164.57, 16.88) * mm, "end": v(-163.8, 17.45) * mm});
            skLineSegment(sketch, "E393", {"start": v(-163.8, 17.45) * mm, "end": v(-161.3, 18.93) * mm});
            skLineSegment(sketch, "E394", {"start": v(-161.3, 18.93) * mm, "end": v(-157.82, 20.54) * mm});
            skLineSegment(sketch, "E395", {"start": v(-157.82, 20.54) * mm, "end": v(-154.34, 21.57) * mm});
            skLineSegment(sketch, "E396", {"start": v(-154.34, 21.57) * mm, "end": v(-151.89, 21.94) * mm});
            skLineSegment(sketch, "E397", {"start": v(-151.89, 21.94) * mm, "end": v(-151.07, 21.94) * mm});
            skLineSegment(sketch, "E398", {"start": v(-151.07, 21.94) * mm, "end": v(-150.74, 21.94) * mm});
            skLineSegment(sketch, "E399", {"start": v(-150.74, 21.94) * mm, "end": v(-149.77, 21.87) * mm});
            skLineSegment(sketch, "E400", {"start": v(-149.77, 21.87) * mm, "end": v(-148.67, 21.65) * mm});
            skLineSegment(sketch, "E401", {"start": v(-148.67, 21.65) * mm, "end": v(-147.76, 21.27) * mm});
            skLineSegment(sketch, "E402", {"start": v(-147.76, 21.27) * mm, "end": v(-147.04, 20.72) * mm});
            skLineSegment(sketch, "E403", {"start": v(-147.04, 20.72) * mm, "end": v(-146.49, 20) * mm});
            skLineSegment(sketch, "E404", {"start": v(-146.49, 20) * mm, "end": v(-146.11, 19.1) * mm});
            skLineSegment(sketch, "E405", {"start": v(-146.11, 19.1) * mm, "end": v(-145.9, 18) * mm});
            skLineSegment(sketch, "E406", {"start": v(-145.9, 18) * mm, "end": v(-145.82, 17.02) * mm});
            skLineSegment(sketch, "E407", {"start": v(-145.82, 17.02) * mm, "end": v(-145.82, 16.7) * mm});
            skLineSegment(sketch, "E408", {"start": v(-145.82, 16.7) * mm, "end": v(-145.82, -46.88) * mm});
            skLineSegment(sketch, "E409", {"start": v(-145.82, -46.88) * mm, "end": v(-123.44, -46.88) * mm});
            skLineSegment(sketch, "E410", {"start": v(-123.44, -46.88) * mm, "end": v(-60.45, -46.93) * mm});
            skLineSegment(sketch, "E411", {"start": v(-60.45, -46.93) * mm, "end": v(-59.11, -46.69) * mm});
            skLineSegment(sketch, "E412", {"start": v(-59.11, -46.69) * mm, "end": v(-55.14, -45.67) * mm});
            skLineSegment(sketch, "E413", {"start": v(-55.14, -45.67) * mm, "end": v(-50.33, -43.85) * mm});
            skLineSegment(sketch, "E414", {"start": v(-50.33, -43.85) * mm, "end": v(-46.08, -41.44) * mm});
            skLineSegment(sketch, "E415", {"start": v(-46.08, -41.44) * mm, "end": v(-42.46, -38.39) * mm});
            skLineSegment(sketch, "E416", {"start": v(-42.46, -38.39) * mm, "end": v(-39.53, -34.67) * mm});
            skLineSegment(sketch, "E417", {"start": v(-39.53, -34.67) * mm, "end": v(-37.35, -30.25) * mm});
            skLineSegment(sketch, "E418", {"start": v(-37.35, -30.25) * mm, "end": v(-36, -25.08) * mm});
            skLineSegment(sketch, "E419", {"start": v(-36, -25.08) * mm, "end": v(-35.54, -20.62) * mm});
            skLineSegment(sketch, "E420", {"start": v(-35.54, -20.62) * mm, "end": v(-35.54, -19.13) * mm});
            skLineSegment(sketch, "E421", {"start": v(-35.54, -19.13) * mm, "end": v(-35.54, -17.98) * mm});
            skLineSegment(sketch, "E422", {"start": v(-35.54, -17.98) * mm, "end": v(-35.84, -14.52) * mm});
            skLineSegment(sketch, "E423", {"start": v(-35.84, -14.52) * mm, "end": v(-36.7, -10.38) * mm});
            skLineSegment(sketch, "E424", {"start": v(-36.7, -10.38) * mm, "end": v(-38.08, -6.7) * mm});
            skLineSegment(sketch, "E425", {"start": v(-38.08, -6.7) * mm, "end": v(-39.92, -3.45) * mm});
            skLineSegment(sketch, "E426", {"start": v(-39.92, -3.45) * mm, "end": v(-42.18, -0.6) * mm});
            skLineSegment(sketch, "E427", {"start": v(-42.18, -0.6) * mm, "end": v(-44.8, 1.84) * mm});
            skLineSegment(sketch, "E428", {"start": v(-44.8, 1.84) * mm, "end": v(-47.73, 3.91) * mm});
            skLineSegment(sketch, "E429", {"start": v(-47.73, 3.91) * mm, "end": v(-50.1, 5.24) * mm});
            skLineSegment(sketch, "E430", {"start": v(-50.1, 5.24) * mm, "end": v(-50.92, 5.62) * mm});
            skLineSegment(sketch, "E431", {"start": v(195.3, 46.88) * mm, "end": v(193.65, 46.88) * mm});
            skLineSegment(sketch, "E432", {"start": v(193.65, 46.88) * mm, "end": v(188.7, 46.5) * mm});
            skLineSegment(sketch, "E433", {"start": v(188.7, 46.5) * mm, "end": v(181.87, 45.22) * mm});
            skLineSegment(sketch, "E434", {"start": v(181.87, 45.22) * mm, "end": v(175.28, 42.85) * mm});
            skLineSegment(sketch, "E435", {"start": v(175.28, 42.85) * mm, "end": v(170.75, 40.28) * mm});
            skLineSegment(sketch, "E436", {"start": v(170.75, 40.28) * mm, "end": v(169.42, 39.2) * mm});
            skLineSegment(sketch, "E437", {"start": v(169.42, 39.2) * mm, "end": v(169.23, 39.2) * mm});
            skLineSegment(sketch, "E438", {"start": v(169.23, 39.2) * mm, "end": v(167.54, 45) * mm});
            skLineSegment(sketch, "E439", {"start": v(167.54, 45) * mm, "end": v(145.6, 45) * mm});
            skLineSegment(sketch, "E440", {"start": v(145.6, 45) * mm, "end": v(145.6, -23.32) * mm});
            skLineSegment(sketch, "E441", {"start": v(145.6, -23.32) * mm, "end": v(130.6, -23.32) * mm});
            skLineSegment(sketch, "E442", {"start": v(130.6, -23.32) * mm, "end": v(130.6, 21.75) * mm});
            skLineSegment(sketch, "E443", {"start": v(130.6, 21.75) * mm, "end": v(130.6, 23.37) * mm});
            skLineSegment(sketch, "E444", {"start": v(130.6, 23.37) * mm, "end": v(129.82, 28.22) * mm});
            skLineSegment(sketch, "E445", {"start": v(129.82, 28.22) * mm, "end": v(127.59, 33.6) * mm});
            skLineSegment(sketch, "E446", {"start": v(127.59, 33.6) * mm, "end": v(124.08, 37.95) * mm});
            skLineSegment(sketch, "E447", {"start": v(124.08, 37.95) * mm, "end": v(119.46, 41.35) * mm});
            skLineSegment(sketch, "E448", {"start": v(119.46, 41.35) * mm, "end": v(113.9, 43.88) * mm});
            skLineSegment(sketch, "E449", {"start": v(113.9, 43.88) * mm, "end": v(107.57, 45.6) * mm});
            skLineSegment(sketch, "E450", {"start": v(107.57, 45.6) * mm, "end": v(100.64, 46.57) * mm});
            skLineSegment(sketch, "E451", {"start": v(100.64, 46.57) * mm, "end": v(95.12, 46.88) * mm});
            skLineSegment(sketch, "E452", {"start": v(95.12, 46.88) * mm, "end": v(93.28, 46.88) * mm});
            skLineSegment(sketch, "E453", {"start": v(93.28, 46.88) * mm, "end": v(91.55, 46.88) * mm});
            skLineSegment(sketch, "E454", {"start": v(91.55, 46.88) * mm, "end": v(86.36, 46.67) * mm});
            skLineSegment(sketch, "E455", {"start": v(86.36, 46.67) * mm, "end": v(78.18, 46) * mm});
            skLineSegment(sketch, "E456", {"start": v(78.18, 46) * mm, "end": v(69.44, 44.82) * mm});
            skLineSegment(sketch, "E457", {"start": v(69.44, 44.82) * mm, "end": v(62.96, 43.64) * mm});
            skLineSegment(sketch, "E458", {"start": v(62.96, 43.64) * mm, "end": v(60.83, 43.13) * mm});
            skLineSegment(sketch, "E459", {"start": v(60.83, 43.13) * mm, "end": v(61.96, 18.94) * mm});
            skLineSegment(sketch, "E460", {"start": v(61.96, 18.94) * mm, "end": v(63.13, 19.19) * mm});
            skLineSegment(sketch, "E461", {"start": v(63.13, 19.19) * mm, "end": v(66.67, 19.85) * mm});
            skLineSegment(sketch, "E462", {"start": v(66.67, 19.85) * mm, "end": v(71.31, 20.6) * mm});
            skLineSegment(sketch, "E463", {"start": v(71.31, 20.6) * mm, "end": v(75.79, 21.22) * mm});
            skLineSegment(sketch, "E464", {"start": v(75.79, 21.22) * mm, "end": v(79.98, 21.7) * mm});
            skLineSegment(sketch, "E465", {"start": v(79.98, 21.7) * mm, "end": v(83.8, 22.07) * mm});
            skLineSegment(sketch, "E466", {"start": v(83.8, 22.07) * mm, "end": v(87.15, 22.32) * mm});
            skLineSegment(sketch, "E467", {"start": v(87.15, 22.32) * mm, "end": v(89.9, 22.46) * mm});
            skLineSegment(sketch, "E468", {"start": v(89.9, 22.46) * mm, "end": v(91.45, 22.5) * mm});
            skLineSegment(sketch, "E469", {"start": v(91.45, 22.5) * mm, "end": v(91.96, 22.5) * mm});
            skLineSegment(sketch, "E470", {"start": v(91.96, 22.5) * mm, "end": v(92.93, 22.5) * mm});
            skLineSegment(sketch, "E471", {"start": v(92.93, 22.5) * mm, "end": v(95.82, 22.18) * mm});
            skLineSegment(sketch, "E472", {"start": v(95.82, 22.18) * mm, "end": v(98.65, 21.08) * mm});
            skLineSegment(sketch, "E473", {"start": v(98.65, 21.08) * mm, "end": v(100.38, 18.94) * mm});
            skLineSegment(sketch, "E474", {"start": v(100.38, 18.94) * mm, "end": v(100.97, 16.4) * mm});
            skLineSegment(sketch, "E475", {"start": v(100.97, 16.4) * mm, "end": v(100.97, 15.57) * mm});
            skLineSegment(sketch, "E476", {"start": v(100.97, 15.57) * mm, "end": v(100.97, 10.5) * mm});
            skLineSegment(sketch, "E477", {"start": v(100.97, 10.5) * mm, "end": v(99.62, 10.5) * mm});
            skLineSegment(sketch, "E478", {"start": v(99.62, 10.5) * mm, "end": v(95.6, 10.4) * mm});
            skLineSegment(sketch, "E479", {"start": v(95.6, 10.4) * mm, "end": v(90.01, 10.1) * mm});
            skLineSegment(sketch, "E480", {"start": v(90.01, 10.1) * mm, "end": v(84.38, 9.5) * mm});
            skLineSegment(sketch, "E481", {"start": v(84.38, 9.5) * mm, "end": v(78.86, 8.6) * mm});
            skLineSegment(sketch, "E482", {"start": v(78.86, 8.6) * mm, "end": v(73.63, 7.34) * mm});
            skLineSegment(sketch, "E483", {"start": v(73.63, 7.34) * mm, "end": v(68.87, 5.68) * mm});
            skLineSegment(sketch, "E484", {"start": v(68.87, 5.68) * mm, "end": v(64.73, 3.56) * mm});
            skLineSegment(sketch, "E485", {"start": v(64.73, 3.56) * mm, "end": v(62.14, 1.68) * mm});
            skLineSegment(sketch, "E486", {"start": v(62.14, 1.68) * mm, "end": v(61.4, 0.94) * mm});
            skLineSegment(sketch, "E487", {"start": v(61.4, 0.94) * mm, "end": v(60.41, -0.04) * mm});
            skLineSegment(sketch, "E488", {"start": v(60.41, -0.04) * mm, "end": v(57.96, -3.5) * mm});
            skLineSegment(sketch, "E489", {"start": v(57.96, -3.5) * mm, "end": v(55.7, -8.46) * mm});
            skLineSegment(sketch, "E490", {"start": v(55.7, -8.46) * mm, "end": v(54.46, -13.75) * mm});
            skLineSegment(sketch, "E491", {"start": v(54.46, -13.75) * mm, "end": v(54.08, -17.79) * mm});
            skLineSegment(sketch, "E492", {"start": v(54.08, -17.79) * mm, "end": v(54.08, -19.13) * mm});
            skLineSegment(sketch, "E493", {"start": v(54.08, -19.13) * mm, "end": v(54.08, -20.8) * mm});
            skLineSegment(sketch, "E494", {"start": v(54.08, -20.8) * mm, "end": v(54.66, -25.83) * mm});
            skLineSegment(sketch, "E495", {"start": v(54.66, -25.83) * mm, "end": v(56.32, -31.6) * mm});
            skLineSegment(sketch, "E496", {"start": v(56.32, -31.6) * mm, "end": v(58.97, -36.44) * mm});
            skLineSegment(sketch, "E497", {"start": v(58.97, -36.44) * mm, "end": v(62.47, -40.38) * mm});
            skLineSegment(sketch, "E498", {"start": v(62.47, -40.38) * mm, "end": v(66.74, -43.44) * mm});
            skLineSegment(sketch, "E499", {"start": v(66.74, -43.44) * mm, "end": v(71.64, -45.64) * mm});
            skLineSegment(sketch, "E500", {"start": v(71.64, -45.64) * mm, "end": v(77.09, -47) * mm});
            skLineSegment(sketch, "E501", {"start": v(77.09, -47) * mm, "end": v(81.5, -47.5) * mm});
            skLineSegment(sketch, "E502", {"start": v(81.5, -47.5) * mm, "end": v(82.96, -47.52) * mm});
            skLineSegment(sketch, "E503", {"start": v(82.96, -47.52) * mm, "end": v(84, -47.54) * mm});
            skLineSegment(sketch, "E504", {"start": v(84, -47.54) * mm, "end": v(87.1, -47.53) * mm});
            skLineSegment(sketch, "E505", {"start": v(87.1, -47.53) * mm, "end": v(92.33, -47.42) * mm});
            skLineSegment(sketch, "E506", {"start": v(92.33, -47.42) * mm, "end": v(98.33, -47.2) * mm});
            skLineSegment(sketch, "E507", {"start": v(98.33, -47.2) * mm, "end": v(103.18, -46.97) * mm});
            skLineSegment(sketch, "E508", {"start": v(103.18, -46.97) * mm, "end": v(104.79, -46.88) * mm});
            skLineSegment(sketch, "E509", {"start": v(104.79, -46.88) * mm, "end": v(145.6, -46.89) * mm});
            skLineSegment(sketch, "E510", {"start": v(145.6, -46.89) * mm, "end": v(145.6, -85.33) * mm});
            skLineSegment(sketch, "E511", {"start": v(145.6, -85.33) * mm, "end": v(175.6, -85.33) * mm});
            skLineSegment(sketch, "E512", {"start": v(175.6, -85.33) * mm, "end": v(175.6, -47.63) * mm});
            skLineSegment(sketch, "E513", {"start": v(175.6, -47.63) * mm, "end": v(176.38, -47.75) * mm});
            skLineSegment(sketch, "E514", {"start": v(176.38, -47.75) * mm, "end": v(178.74, -48) * mm});
            skLineSegment(sketch, "E515", {"start": v(178.74, -48) * mm, "end": v(182.27, -48.22) * mm});
            skLineSegment(sketch, "E516", {"start": v(182.27, -48.22) * mm, "end": v(185.79, -48.35) * mm});
            skLineSegment(sketch, "E517", {"start": v(185.79, -48.35) * mm, "end": v(188.14, -48.39) * mm});
            skLineSegment(sketch, "E518", {"start": v(188.14, -48.39) * mm, "end": v(188.93, -48.39) * mm});
            skLineSegment(sketch, "E519", {"start": v(188.93, -48.39) * mm, "end": v(190.16, -48.39) * mm});
            skLineSegment(sketch, "E520", {"start": v(190.16, -48.39) * mm, "end": v(193.85, -48.2) * mm});
            skLineSegment(sketch, "E521", {"start": v(193.85, -48.2) * mm, "end": v(198.44, -47.64) * mm});
            skLineSegment(sketch, "E522", {"start": v(198.44, -47.64) * mm, "end": v(202.69, -46.7) * mm});
            skLineSegment(sketch, "E523", {"start": v(202.69, -46.7) * mm, "end": v(206.6, -45.39) * mm});
            skLineSegment(sketch, "E524", {"start": v(206.6, -45.39) * mm, "end": v(210.2, -43.7) * mm});
            skLineSegment(sketch, "E525", {"start": v(210.2, -43.7) * mm, "end": v(213.45, -41.63) * mm});
            skLineSegment(sketch, "E526", {"start": v(213.45, -41.63) * mm, "end": v(216.4, -39.19) * mm});
            skLineSegment(sketch, "E527", {"start": v(216.4, -39.19) * mm, "end": v(219, -36.36) * mm});
            skLineSegment(sketch, "E528", {"start": v(219, -36.36) * mm, "end": v(221.3, -33.15) * mm});
            skLineSegment(sketch, "E529", {"start": v(221.3, -33.15) * mm, "end": v(223.27, -29.57) * mm});
            skLineSegment(sketch, "E530", {"start": v(223.27, -29.57) * mm, "end": v(224.94, -25.6) * mm});
            skLineSegment(sketch, "E531", {"start": v(224.94, -25.6) * mm, "end": v(226.3, -21.25) * mm});
            skLineSegment(sketch, "E532", {"start": v(226.3, -21.25) * mm, "end": v(227.35, -16.51) * mm});
            skLineSegment(sketch, "E533", {"start": v(227.35, -16.51) * mm, "end": v(228.09, -11.4) * mm});
            skLineSegment(sketch, "E534", {"start": v(228.09, -11.4) * mm, "end": v(228.53, -5.9) * mm});
            skLineSegment(sketch, "E535", {"start": v(228.53, -5.9) * mm, "end": v(228.69, -1.47) * mm});
            skLineSegment(sketch, "E536", {"start": v(228.69, -1.47) * mm, "end": v(228.69, 0) * mm});
            skLineSegment(sketch, "E537", {"start": v(228.69, 0) * mm, "end": v(228.69, 1.17) * mm});
            skLineSegment(sketch, "E538", {"start": v(228.69, 1.17) * mm, "end": v(228.6, 4.7) * mm});
            skLineSegment(sketch, "E539", {"start": v(228.6, 4.7) * mm, "end": v(228.35, 9.28) * mm});
            skLineSegment(sketch, "E540", {"start": v(228.35, 9.28) * mm, "end": v(227.9, 13.73) * mm});
            skLineSegment(sketch, "E541", {"start": v(227.9, 13.73) * mm, "end": v(227.24, 18) * mm});
            skLineSegment(sketch, "E542", {"start": v(227.24, 18) * mm, "end": v(226.34, 22.1) * mm});
            skLineSegment(sketch, "E543", {"start": v(226.34, 22.1) * mm, "end": v(225.2, 25.96) * mm});
            skLineSegment(sketch, "E544", {"start": v(225.2, 25.96) * mm, "end": v(223.77, 29.58) * mm});
            skLineSegment(sketch, "E545", {"start": v(223.77, 29.58) * mm, "end": v(222.05, 32.94) * mm});
            skLineSegment(sketch, "E546", {"start": v(222.05, 32.94) * mm, "end": v(220.02, 36) * mm});
            skLineSegment(sketch, "E547", {"start": v(220.02, 36) * mm, "end": v(217.65, 38.73) * mm});
            skLineSegment(sketch, "E548", {"start": v(217.65, 38.73) * mm, "end": v(214.92, 41.11) * mm});
            skLineSegment(sketch, "E549", {"start": v(214.92, 41.11) * mm, "end": v(211.83, 43.12) * mm});
            skLineSegment(sketch, "E550", {"start": v(211.83, 43.12) * mm, "end": v(208.34, 44.73) * mm});
            skLineSegment(sketch, "E551", {"start": v(208.34, 44.73) * mm, "end": v(204.43, 45.9) * mm});
            skLineSegment(sketch, "E552", {"start": v(204.43, 45.9) * mm, "end": v(200.1, 46.64) * mm});
            skLineSegment(sketch, "E553", {"start": v(200.1, 46.64) * mm, "end": v(196.5, 46.88) * mm});
            skLineSegment(sketch, "E554", {"start": v(196.5, 46.88) * mm, "end": v(195.3, 46.88) * mm});
            skLineSegment(sketch, "E555", {"start": v(101.34, -22.5) * mm, "end": v(100.89, -22.91) * mm});
            skLineSegment(sketch, "E556", {"start": v(100.89, -22.91) * mm, "end": v(99.32, -23.9) * mm});
            skLineSegment(sketch, "E557", {"start": v(99.32, -23.9) * mm, "end": v(96.86, -24.96) * mm});
            skLineSegment(sketch, "E558", {"start": v(96.86, -24.96) * mm, "end": v(94.3, -25.64) * mm});
            skLineSegment(sketch, "E559", {"start": v(94.3, -25.64) * mm, "end": v(92.55, -25.88) * mm});
            skLineSegment(sketch, "E560", {"start": v(92.55, -25.88) * mm, "end": v(91.96, -25.88) * mm});
            skLineSegment(sketch, "E561", {"start": v(91.96, -25.88) * mm, "end": v(91.05, -25.88) * mm});
            skLineSegment(sketch, "E562", {"start": v(91.05, -25.88) * mm, "end": v(88.3, -25.32) * mm});
            skLineSegment(sketch, "E563", {"start": v(88.3, -25.32) * mm, "end": v(85.73, -23.63) * mm});
            skLineSegment(sketch, "E564", {"start": v(85.73, -23.63) * mm, "end": v(84.2, -20.82) * mm});
            skLineSegment(sketch, "E565", {"start": v(84.2, -20.82) * mm, "end": v(83.7, -17.86) * mm});
            skLineSegment(sketch, "E566", {"start": v(83.7, -17.86) * mm, "end": v(83.7, -16.88) * mm});
            skLineSegment(sketch, "E567", {"start": v(83.7, -16.88) * mm, "end": v(83.7, -16.63) * mm});
            skLineSegment(sketch, "E568", {"start": v(83.7, -16.63) * mm, "end": v(83.76, -15.87) * mm});
            skLineSegment(sketch, "E569", {"start": v(83.76, -15.87) * mm, "end": v(84.02, -14.44) * mm});
            skLineSegment(sketch, "E570", {"start": v(84.02, -14.44) * mm, "end": v(84.58, -12.87) * mm});
            skLineSegment(sketch, "E571", {"start": v(84.58, -12.87) * mm, "end": v(85.28, -11.74) * mm});
            skLineSegment(sketch, "E572", {"start": v(85.28, -11.74) * mm, "end": v(85.59, -11.44) * mm});
            skLineSegment(sketch, "E573", {"start": v(85.59, -11.44) * mm, "end": v(86.1, -10.93) * mm});
            skLineSegment(sketch, "E574", {"start": v(86.1, -10.93) * mm, "end": v(88.15, -9.9) * mm});
            skLineSegment(sketch, "E575", {"start": v(88.15, -9.9) * mm, "end": v(91.77, -9.05) * mm});
            skLineSegment(sketch, "E576", {"start": v(91.77, -9.05) * mm, "end": v(96.24, -8.7) * mm});
            skLineSegment(sketch, "E577", {"start": v(96.24, -8.7) * mm, "end": v(100.06, -8.63) * mm});
            skLineSegment(sketch, "E578", {"start": v(100.06, -8.63) * mm, "end": v(101.34, -8.63) * mm});
            skLineSegment(sketch, "E579", {"start": v(101.34, -8.63) * mm, "end": v(101.34, -22.5) * mm});
            skLineSegment(sketch, "E580", {"start": v(184.42, -24.13) * mm, "end": v(183.88, -24.17) * mm});
            skLineSegment(sketch, "E581", {"start": v(183.88, -24.17) * mm, "end": v(182.26, -24.21) * mm});
            skLineSegment(sketch, "E582", {"start": v(182.26, -24.21) * mm, "end": v(179.88, -24.13) * mm});
            skLineSegment(sketch, "E583", {"start": v(179.88, -24.13) * mm, "end": v(177.57, -23.86) * mm});
            skLineSegment(sketch, "E584", {"start": v(177.57, -23.86) * mm, "end": v(176.08, -23.56) * mm});
            skLineSegment(sketch, "E585", {"start": v(176.08, -23.56) * mm, "end": v(175.6, -23.4) * mm});
            skLineSegment(sketch, "E586", {"start": v(175.6, -23.4) * mm, "end": v(175.6, 18.57) * mm});
            skLineSegment(sketch, "E587", {"start": v(175.6, 18.57) * mm, "end": v(176.1, 18.95) * mm});
            skLineSegment(sketch, "E588", {"start": v(176.1, 18.95) * mm, "end": v(177.73, 19.94) * mm});
            skLineSegment(sketch, "E589", {"start": v(177.73, 19.94) * mm, "end": v(180.39, 21.15) * mm});
            skLineSegment(sketch, "E590", {"start": v(180.39, 21.15) * mm, "end": v(183.47, 22) * mm});
            skLineSegment(sketch, "E591", {"start": v(183.47, 22) * mm, "end": v(186.01, 22.32) * mm});
            skLineSegment(sketch, "E592", {"start": v(186.01, 22.32) * mm, "end": v(186.86, 22.32) * mm});
            skLineSegment(sketch, "E593", {"start": v(186.86, 22.32) * mm, "end": v(187.49, 22.32) * mm});
            skLineSegment(sketch, "E594", {"start": v(187.49, 22.32) * mm, "end": v(189.36, 22.1) * mm});
            skLineSegment(sketch, "E595", {"start": v(189.36, 22.1) * mm, "end": v(191.54, 21.37) * mm});
            skLineSegment(sketch, "E596", {"start": v(191.54, 21.37) * mm, "end": v(193.38, 19.99) * mm});
            skLineSegment(sketch, "E597", {"start": v(193.38, 19.99) * mm, "end": v(194.88, 17.82) * mm});
            skLineSegment(sketch, "E598", {"start": v(194.88, 17.82) * mm, "end": v(196.05, 14.74) * mm});
            skLineSegment(sketch, "E599", {"start": v(196.05, 14.74) * mm, "end": v(196.88, 10.6) * mm});
            skLineSegment(sketch, "E600", {"start": v(196.88, 10.6) * mm, "end": v(197.38, 5.3) * mm});
            skLineSegment(sketch, "E601", {"start": v(197.38, 5.3) * mm, "end": v(197.55, 0.34) * mm});
            skLineSegment(sketch, "E602", {"start": v(197.55, 0.34) * mm, "end": v(197.55, -1.31) * mm});
            skLineSegment(sketch, "E603", {"start": v(197.55, -1.31) * mm, "end": v(197.55, -2.68) * mm});
            skLineSegment(sketch, "E604", {"start": v(197.55, -2.68) * mm, "end": v(197.39, -6.78) * mm});
            skLineSegment(sketch, "E605", {"start": v(197.39, -6.78) * mm, "end": v(196.88, -11.4) * mm});
            skLineSegment(sketch, "E606", {"start": v(196.88, -11.4) * mm, "end": v(196, -15.23) * mm});
            skLineSegment(sketch, "E607", {"start": v(196, -15.23) * mm, "end": v(194.68, -18.3) * mm});
            skLineSegment(sketch, "E608", {"start": v(194.68, -18.3) * mm, "end": v(192.91, -20.68) * mm});
            skLineSegment(sketch, "E609", {"start": v(192.91, -20.68) * mm, "end": v(190.63, -22.4) * mm});
            skLineSegment(sketch, "E610", {"start": v(190.63, -22.4) * mm, "end": v(187.82, -23.54) * mm});
            skLineSegment(sketch, "E611", {"start": v(187.82, -23.54) * mm, "end": v(185.28, -24.05) * mm});
            skLineSegment(sketch, "E612", {"start": v(185.28, -24.05) * mm, "end": v(184.42, -24.13) * mm});
            skLineSegment(sketch, "E613.bottom", {"start": v(-329.88, 104.38) * mm, "end": v(329.88, 104.38) * mm});
            skLineSegment(sketch, "E613.top", {"start": v(-329.88, -98.82) * mm, "end": v(329.88, -98.82) * mm});
            skLineSegment(sketch, "E613.left", {"start": v(-329.88, 104.38) * mm, "end": v(-329.88, -98.82) * mm});
            skLineSegment(sketch, "E613.right", {"start": v(329.88, 104.38) * mm, "end": v(329.88, -98.82) * mm});
            skSolve(sketch);
        }
        {
            var Q0;
            Q0=makeQuery(id+"F3.imprint","IMPRINT",FACE,{"disambiguationData":[TD([[makeQuery(id+"F3.imprint","IMPRINT",EDGE,{"derivedFrom":sQuery(id+"F3.wireOp",EDGE,"E0")}),1.0]])]});
            var Q1;
            Q1=makeQuery(id+"F3.imprint","IMPRINT",FACE,{"disambiguationData":[TD([[makeQuery(id+"F3.imprint","IMPRINT",EDGE,{"derivedFrom":sQuery(id+"F3.wireOp",EDGE,"E290")}),1.0]])]});
            var Q2;
            Q2=makeQuery(id+"F3.imprint","IMPRINT",FACE,{"disambiguationData":[TD([[makeQuery(id+"F3.imprint","IMPRINT",EDGE,{"derivedFrom":sQuery(id+"F3.wireOp",EDGE,"E144")}),1.0]])]});
            var Q3;
            Q3=makeQuery(id+"F3.imprint","IMPRINT",FACE,{"disambiguationData":[TD([[makeQuery(id+"F3.imprint","IMPRINT",EDGE,{"derivedFrom":sQuery(id+"F3.wireOp",EDGE,"E431")}),1.0]])]});
            var Q4;
            Q4=makeQuery(id+"F3.imprint","IMPRINT",FACE,{"disambiguationData":[TD([[makeQuery(id+"F3.imprint","IMPRINT",EDGE,{"derivedFrom":sQuery(id+"F3.wireOp",EDGE,"E185")}),1.0]])]});
            extrude(context, id + "F4", {"entities" : qUnion([Q0, Q1, Q2, Q3, Q4]), "depth" : getVariable(context, 'letterHeight') / getVariable(context, 'scaleFactor')});
        }
        {
            var Q0;
            Q0=makeQuery(id+"F3.imprint","IMPRINT",FACE,{"disambiguationData":[TD([[makeQuery(id+"F3.imprint","IMPRINT",EDGE,{"derivedFrom":sQuery(id+"F3.wireOp",EDGE,"E0")}),-1.0]])]});
            var Q1;
            Q1=makeQuery(id+"F3.imprint","IMPRINT",FACE,{"disambiguationData":[TD([[makeQuery(id+"F3.imprint","IMPRINT",EDGE,{"derivedFrom":sQuery(id+"F3.wireOp",EDGE,"E72")}),-1.0]])]});
            var Q2;
            Q2=makeQuery(id+"F3.imprint","IMPRINT",FACE,{"disambiguationData":[TD([[makeQuery(id+"F3.imprint","IMPRINT",EDGE,{"derivedFrom":sQuery(id+"F3.wireOp",EDGE,"E555")}),-1.0]])]});
            var Q3;
            Q3=makeQuery(id+"F3.imprint","IMPRINT",FACE,{"disambiguationData":[TD([[makeQuery(id+"F3.imprint","IMPRINT",EDGE,{"derivedFrom":sQuery(id+"F3.wireOp",EDGE,"E580")}),-1.0]])]});
            var Q4;
            Q4=makeQuery(id+"F3.imprint","IMPRINT",FACE,{"disambiguationData":[TD([[makeQuery(id+"F3.imprint","IMPRINT",EDGE,{"derivedFrom":sQuery(id+"F3.wireOp",EDGE,"E268")}),-1.0]])]});
            extrude(context, id + "F5", {"entities" : qUnion([Q0, Q1, Q2, Q3, Q4]), "operationType" : NewBodyOperationType.ADD, "depth" : getVariable(context, 'plateHeight') / getVariable(context, 'scaleFactor')});
        }
        {
            var Q0;
            Q0=makeQuery(id+"F4.opExtrude","SWEPT_BODY",BODY,{"disambiguationData":[OSD([sQuery(id+"F3.wireOp",EDGE,"E0"),sQuery(id+"F3.wireOp",EDGE,"E1"),sQuery(id+"F3.wireOp",EDGE,"E2"),sQuery(id+"F3.wireOp",EDGE,"E3"),sQuery(id+"F3.wireOp",EDGE,"E4"),sQuery(id+"F3.wireOp",EDGE,"E5"),sQuery(id+"F3.wireOp",EDGE,"E6"),sQuery(id+"F3.wireOp",EDGE,"E7"),sQuery(id+"F3.wireOp",EDGE,"E8"),sQuery(id+"F3.wireOp",EDGE,"E9"),sQuery(id+"F3.wireOp",EDGE,"E10"),sQuery(id+"F3.wireOp",EDGE,"E11"),sQuery(id+"F3.wireOp",EDGE,"E12"),sQuery(id+"F3.wireOp",EDGE,"E13"),sQuery(id+"F3.wireOp",EDGE,"E14"),sQuery(id+"F3.wireOp",EDGE,"E15"),sQuery(id+"F3.wireOp",EDGE,"E16"),sQuery(id+"F3.wireOp",EDGE,"E17"),sQuery(id+"F3.wireOp",EDGE,"E18"),sQuery(id+"F3.wireOp",EDGE,"E19"),sQuery(id+"F3.wireOp",EDGE,"E20"),sQuery(id+"F3.wireOp",EDGE,"E21"),sQuery(id+"F3.wireOp",EDGE,"E22"),sQuery(id+"F3.wireOp",EDGE,"E23"),sQuery(id+"F3.wireOp",EDGE,"E24"),sQuery(id+"F3.wireOp",EDGE,"E25"),sQuery(id+"F3.wireOp",EDGE,"E26"),sQuery(id+"F3.wireOp",EDGE,"E27"),sQuery(id+"F3.wireOp",EDGE,"E28"),sQuery(id+"F3.wireOp",EDGE,"E29"),sQuery(id+"F3.wireOp",EDGE,"E30"),sQuery(id+"F3.wireOp",EDGE,"E31"),sQuery(id+"F3.wireOp",EDGE,"E32"),sQuery(id+"F3.wireOp",EDGE,"E33"),sQuery(id+"F3.wireOp",EDGE,"E34"),sQuery(id+"F3.wireOp",EDGE,"E35"),sQuery(id+"F3.wireOp",EDGE,"E36"),sQuery(id+"F3.wireOp",EDGE,"E37"),sQuery(id+"F3.wireOp",EDGE,"E38"),sQuery(id+"F3.wireOp",EDGE,"E39"),sQuery(id+"F3.wireOp",EDGE,"E40"),sQuery(id+"F3.wireOp",EDGE,"E41"),sQuery(id+"F3.wireOp",EDGE,"E42"),sQuery(id+"F3.wireOp",EDGE,"E43"),sQuery(id+"F3.wireOp",EDGE,"E44"),sQuery(id+"F3.wireOp",EDGE,"E45"),sQuery(id+"F3.wireOp",EDGE,"E46"),sQuery(id+"F3.wireOp",EDGE,"E47"),sQuery(id+"F3.wireOp",EDGE,"E48"),sQuery(id+"F3.wireOp",EDGE,"E49"),sQuery(id+"F3.wireOp",EDGE,"E50"),sQuery(id+"F3.wireOp",EDGE,"E51"),sQuery(id+"F3.wireOp",EDGE,"E52"),sQuery(id+"F3.wireOp",EDGE,"E53"),sQuery(id+"F3.wireOp",EDGE,"E54"),sQuery(id+"F3.wireOp",EDGE,"E55"),sQuery(id+"F3.wireOp",EDGE,"E56"),sQuery(id+"F3.wireOp",EDGE,"E57"),sQuery(id+"F3.wireOp",EDGE,"E58"),sQuery(id+"F3.wireOp",EDGE,"E59"),sQuery(id+"F3.wireOp",EDGE,"E60"),sQuery(id+"F3.wireOp",EDGE,"E61"),sQuery(id+"F3.wireOp",EDGE,"E62"),sQuery(id+"F3.wireOp",EDGE,"E63"),sQuery(id+"F3.wireOp",EDGE,"E64"),sQuery(id+"F3.wireOp",EDGE,"E65"),sQuery(id+"F3.wireOp",EDGE,"E66"),sQuery(id+"F3.wireOp",EDGE,"E67"),sQuery(id+"F3.wireOp",EDGE,"E68"),sQuery(id+"F3.wireOp",EDGE,"E69"),sQuery(id+"F3.wireOp",EDGE,"E70"),sQuery(id+"F3.wireOp",EDGE,"E71"),sQuery(id+"F3.wireOp",EDGE,"E72"),sQuery(id+"F3.wireOp",EDGE,"E73"),sQuery(id+"F3.wireOp",EDGE,"E74"),sQuery(id+"F3.wireOp",EDGE,"E75"),sQuery(id+"F3.wireOp",EDGE,"E76"),sQuery(id+"F3.wireOp",EDGE,"E77"),sQuery(id+"F3.wireOp",EDGE,"E78"),sQuery(id+"F3.wireOp",EDGE,"E79"),sQuery(id+"F3.wireOp",EDGE,"E80"),sQuery(id+"F3.wireOp",EDGE,"E81"),sQuery(id+"F3.wireOp",EDGE,"E82"),sQuery(id+"F3.wireOp",EDGE,"E83"),sQuery(id+"F3.wireOp",EDGE,"E84"),sQuery(id+"F3.wireOp",EDGE,"E85"),sQuery(id+"F3.wireOp",EDGE,"E86"),sQuery(id+"F3.wireOp",EDGE,"E87"),sQuery(id+"F3.wireOp",EDGE,"E88"),sQuery(id+"F3.wireOp",EDGE,"E89"),sQuery(id+"F3.wireOp",EDGE,"E90"),sQuery(id+"F3.wireOp",EDGE,"E91"),sQuery(id+"F3.wireOp",EDGE,"E92"),sQuery(id+"F3.wireOp",EDGE,"E93"),sQuery(id+"F3.wireOp",EDGE,"E94"),sQuery(id+"F3.wireOp",EDGE,"E95"),sQuery(id+"F3.wireOp",EDGE,"E96"),sQuery(id+"F3.wireOp",EDGE,"E97"),sQuery(id+"F3.wireOp",EDGE,"E98"),sQuery(id+"F3.wireOp",EDGE,"E99"),sQuery(id+"F3.wireOp",EDGE,"E100"),sQuery(id+"F3.wireOp",EDGE,"E101"),sQuery(id+"F3.wireOp",EDGE,"E102"),sQuery(id+"F3.wireOp",EDGE,"E103"),sQuery(id+"F3.wireOp",EDGE,"E104"),sQuery(id+"F3.wireOp",EDGE,"E105"),sQuery(id+"F3.wireOp",EDGE,"E106"),sQuery(id+"F3.wireOp",EDGE,"E107"),sQuery(id+"F3.wireOp",EDGE,"E108"),sQuery(id+"F3.wireOp",EDGE,"E109"),sQuery(id+"F3.wireOp",EDGE,"E110"),sQuery(id+"F3.wireOp",EDGE,"E111"),sQuery(id+"F3.wireOp",EDGE,"E112"),sQuery(id+"F3.wireOp",EDGE,"E113"),sQuery(id+"F3.wireOp",EDGE,"E114"),sQuery(id+"F3.wireOp",EDGE,"E115"),sQuery(id+"F3.wireOp",EDGE,"E116"),sQuery(id+"F3.wireOp",EDGE,"E117"),sQuery(id+"F3.wireOp",EDGE,"E118"),sQuery(id+"F3.wireOp",EDGE,"E119"),sQuery(id+"F3.wireOp",EDGE,"E120"),sQuery(id+"F3.wireOp",EDGE,"E121"),sQuery(id+"F3.wireOp",EDGE,"E122"),sQuery(id+"F3.wireOp",EDGE,"E123"),sQuery(id+"F3.wireOp",EDGE,"E124"),sQuery(id+"F3.wireOp",EDGE,"E125"),sQuery(id+"F3.wireOp",EDGE,"E126"),sQuery(id+"F3.wireOp",EDGE,"E127"),sQuery(id+"F3.wireOp",EDGE,"E128"),sQuery(id+"F3.wireOp",EDGE,"E129"),sQuery(id+"F3.wireOp",EDGE,"E130"),sQuery(id+"F3.wireOp",EDGE,"E131"),sQuery(id+"F3.wireOp",EDGE,"E132"),sQuery(id+"F3.wireOp",EDGE,"E133"),sQuery(id+"F3.wireOp",EDGE,"E134"),sQuery(id+"F3.wireOp",EDGE,"E135"),sQuery(id+"F3.wireOp",EDGE,"E136"),sQuery(id+"F3.wireOp",EDGE,"E137"),sQuery(id+"F3.wireOp",EDGE,"E138"),sQuery(id+"F3.wireOp",EDGE,"E139"),sQuery(id+"F3.wireOp",EDGE,"E140"),sQuery(id+"F3.wireOp",EDGE,"E141"),sQuery(id+"F3.wireOp",EDGE,"E142"),sQuery(id+"F3.wireOp",EDGE,"E143")])]});
            var Q1;
            Q1=qCreatedBy(makeId("Origin.pointOp"),VERTEX);
            transform(context, id + "F6", {"entities" : qUnion([Q0]), "transformType" : TransformType.SCALE_UNIFORMLY, "scale" : getVariable(context, 'scaleFactor'), "scalePoint" : qUnion([Q1]), "makeCopy" : false});
        }
    });
